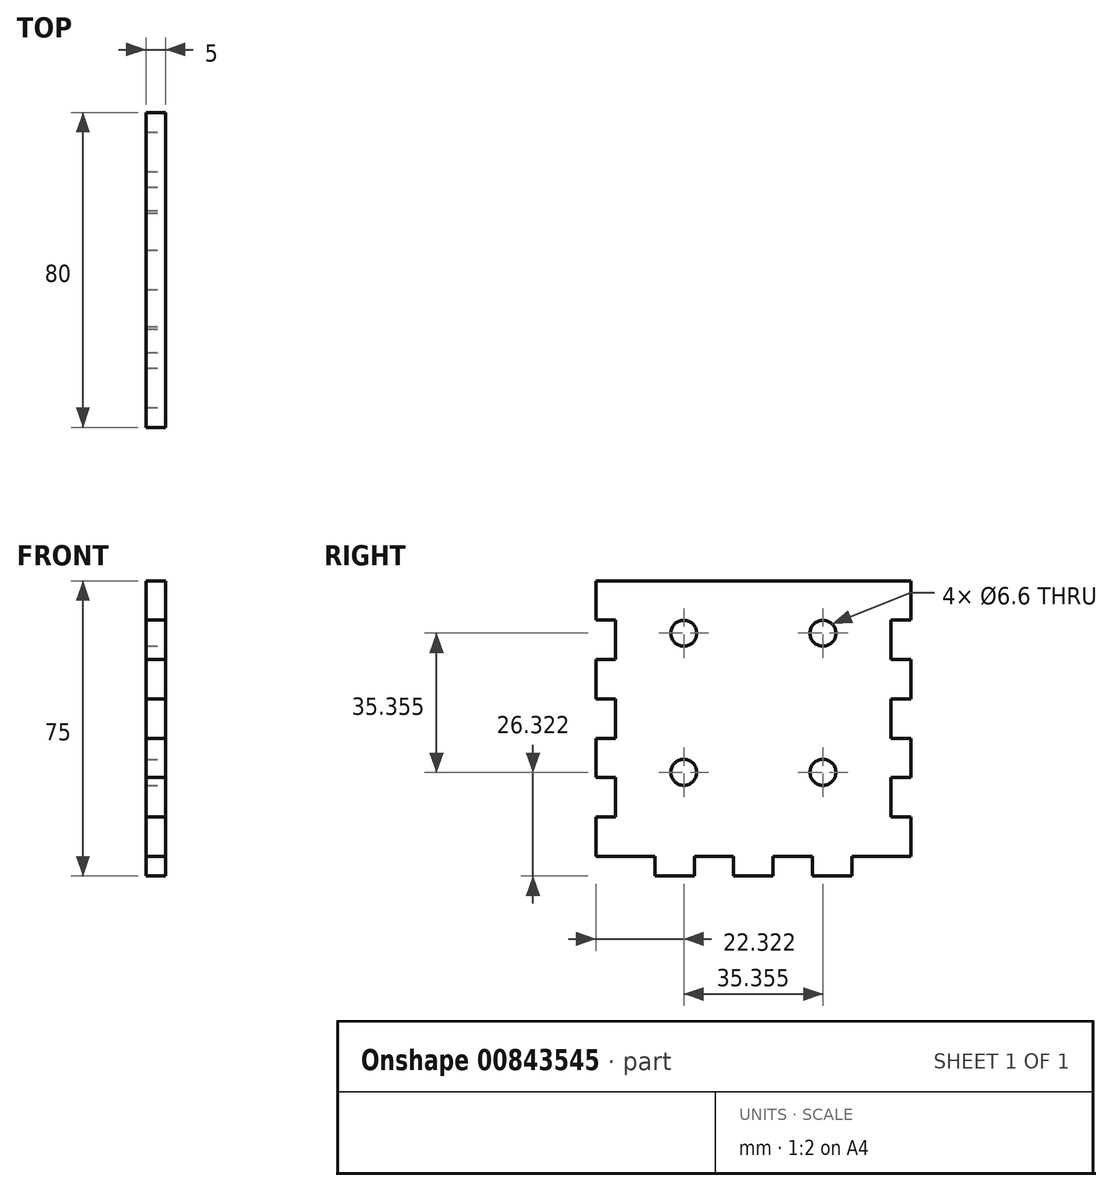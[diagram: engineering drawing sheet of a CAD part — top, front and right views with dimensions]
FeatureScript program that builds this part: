
annotation { "Feature Type Name" : "Feature", "Feature Type Description" : "" }
export const myFeature = defineFeature(function(context is Context, id is Id, definition is map)
    precondition{}
    {
        {
            var Q0;
            Q0=qCreatedBy(makeId("Right.planeOp"),FACE);
            var sketch = newSketch(context, id + "F0", { "sketchPlane" : qUnion([Q0])});
            skLineSegment(sketch, "E0.bottom", {"start": v(35, 35) * mm, "end": v(-35, 35) * mm});
            skLineSegment(sketch, "E0.top", {"start": v(35, -35) * mm, "end": v(-35, -35) * mm});
            skLineSegment(sketch, "E0.left", {"start": v(35, 35) * mm, "end": v(35, -35) * mm});
            skLineSegment(sketch, "E0.right", {"start": v(-35, 35) * mm, "end": v(-35, -35) * mm});
            skPoint(sketch, "E0.middle", {"position": v(0, 0) * mm});
            skSolve(sketch);
        }
        {
            var Q0;
            Q0 = qSketchRegion(id + "F0", true);
            extrude(context, id + "F1", {"entities" : qUnion([Q0]), "endBound" : BoundingType.SYMMETRIC, "depth" : 5 * mm, "offsetDistance" : 25 * mm});
        }
        {
            var Q0;
            Q0=makeQuery(id+"F1.opExtrude","CAP_FACE",FACE,{"disambiguationData":[OSD([sQuery(id+"F0.wireOp",EDGE,"E0.bottom"),sQuery(id+"F0.wireOp",EDGE,"E0.top"),sQuery(id+"F0.wireOp",EDGE,"E0.left"),sQuery(id+"F0.wireOp",EDGE,"E0.right")])],"isStart":false});
            var sketch = newSketch(context, id + "F2", { "sketchPlane" : qUnion([Q0])});
            skLineSegment(sketch, "E1.bottom", {"start": v(-25, -35) * mm, "end": v(-15, -35) * mm});
            skLineSegment(sketch, "E1.top", {"start": v(-25, -40) * mm, "end": v(-15, -40) * mm});
            skLineSegment(sketch, "E1.left", {"start": v(-25, -35) * mm, "end": v(-25, -40) * mm});
            skLineSegment(sketch, "E1.right", {"start": v(-15, -35) * mm, "end": v(-15, -40) * mm});
            skLineSegment(sketch, "E2.1.0.0", {"start": v(5, -35) * mm, "end": v(5, -40) * mm});
            skLineSegment(sketch, "E2.1.0.1", {"start": v(-5, -35) * mm, "end": v(-5, -40) * mm});
            skLineSegment(sketch, "E2.1.0.2", {"start": v(-5, -40) * mm, "end": v(5, -40) * mm});
            skLineSegment(sketch, "E2.1.0.3", {"start": v(-5, -35) * mm, "end": v(5, -35) * mm});
            skLineSegment(sketch, "E2.2.0.0", {"start": v(25, -35) * mm, "end": v(25, -40) * mm});
            skLineSegment(sketch, "E2.2.0.1", {"start": v(15, -35) * mm, "end": v(15, -40) * mm});
            skLineSegment(sketch, "E2.2.0.2", {"start": v(15, -40) * mm, "end": v(25, -40) * mm});
            skLineSegment(sketch, "E2.2.0.3", {"start": v(15, -35) * mm, "end": v(25, -35) * mm});
            skLineSegment(sketch, "E2.direction1", {"start": v(-25, -40) * mm, "end": v(-5, -40) * mm, "construction": true});
            skSolve(sketch);
        }
        {
            var Q0;
            Q0 = qSketchRegion(id + "F2", true);
            extrude(context, id + "F3", {"entities" : qUnion([Q0]), "operationType" : NewBodyOperationType.ADD, "oppositeDirection" : true, "depth" : 5 * mm, "offsetDistance" : 25 * mm});
        }
        {
            var Q0;
            {var subQ1=sQuery(id+"F2.wireOp",EDGE,"E1.bottom");Q0=makeQuery(id+"F2.imprint","IMPRINT",FACE,{"disambiguationData":[TD([[makeQuery(id+"F2.imprint","IMPRINT",EDGE,{"derivedFrom":subQ1}),-1.0]])]});}
            var sketch = newSketch(context, id + "F4", { "sketchPlane" : qUnion([Q0])});
            skLineSegment(sketch, "E3.bottom", {"start": v(-35, -35) * mm, "end": v(-40, -35) * mm});
            skLineSegment(sketch, "E3.top", {"start": v(-35, -25) * mm, "end": v(-40, -25) * mm});
            skLineSegment(sketch, "E3.left", {"start": v(-35, -35) * mm, "end": v(-35, -25) * mm});
            skLineSegment(sketch, "E3.right", {"start": v(-40, -35) * mm, "end": v(-40, -25) * mm});
            skLineSegment(sketch, "E4.0.1.0", {"start": v(-35, -15) * mm, "end": v(-35, -5) * mm});
            skLineSegment(sketch, "E4.0.1.1", {"start": v(-40, -15) * mm, "end": v(-40, -5) * mm});
            skLineSegment(sketch, "E4.0.1.2", {"start": v(-35, -15) * mm, "end": v(-40, -15) * mm});
            skLineSegment(sketch, "E4.0.1.3", {"start": v(-35, -5) * mm, "end": v(-40, -5) * mm});
            skLineSegment(sketch, "E4.0.2.0", {"start": v(-35, 5) * mm, "end": v(-35, 15) * mm});
            skLineSegment(sketch, "E4.0.2.1", {"start": v(-40, 5) * mm, "end": v(-40, 15) * mm});
            skLineSegment(sketch, "E4.0.2.2", {"start": v(-35, 5) * mm, "end": v(-40, 5) * mm});
            skLineSegment(sketch, "E4.0.2.3", {"start": v(-35, 15) * mm, "end": v(-40, 15) * mm});
            skLineSegment(sketch, "E4.0.3.0", {"start": v(-35, 25) * mm, "end": v(-35, 35) * mm});
            skLineSegment(sketch, "E4.0.3.1", {"start": v(-40, 25) * mm, "end": v(-40, 35) * mm});
            skLineSegment(sketch, "E4.0.3.2", {"start": v(-35, 25) * mm, "end": v(-40, 25) * mm});
            skLineSegment(sketch, "E4.0.3.3", {"start": v(-35, 35) * mm, "end": v(-40, 35) * mm});
            skLineSegment(sketch, "E4.direction1", {"start": v(-40, -35) * mm, "end": v(-15, -35) * mm, "construction": true});
            skLineSegment(sketch, "E4.direction2", {"start": v(-40, -35) * mm, "end": v(-40, -15) * mm, "construction": true});
            skLineSegment(sketch, "E5.1.0.0", {"start": v(40, 25) * mm, "end": v(40, 35) * mm});
            skLineSegment(sketch, "E5.1.0.1", {"start": v(40, 25) * mm, "end": v(35, 25) * mm});
            skLineSegment(sketch, "E5.1.0.2", {"start": v(40, -35) * mm, "end": v(35, -35) * mm});
            skLineSegment(sketch, "E5.1.0.3", {"start": v(40, 15) * mm, "end": v(35, 15) * mm});
            skLineSegment(sketch, "E5.1.0.4", {"start": v(40, -35) * mm, "end": v(40, -25) * mm});
            skLineSegment(sketch, "E5.1.0.5", {"start": v(35, -35) * mm, "end": v(35, -15) * mm, "construction": true});
            skLineSegment(sketch, "E5.1.0.6", {"start": v(40, 5) * mm, "end": v(40, 15) * mm});
            skLineSegment(sketch, "E5.1.0.7", {"start": v(40, -15) * mm, "end": v(40, -5) * mm});
            skLineSegment(sketch, "E5.1.0.8", {"start": v(40, -15) * mm, "end": v(35, -15) * mm});
            skLineSegment(sketch, "E5.1.0.9", {"start": v(35, 5) * mm, "end": v(35, 15) * mm});
            skLineSegment(sketch, "E5.1.0.10", {"start": v(40, 35) * mm, "end": v(35, 35) * mm});
            skLineSegment(sketch, "E5.1.0.11", {"start": v(40, -25) * mm, "end": v(35, -25) * mm});
            skLineSegment(sketch, "E5.1.0.12", {"start": v(35, -15) * mm, "end": v(35, -5) * mm});
            skLineSegment(sketch, "E5.1.0.13", {"start": v(40, 5) * mm, "end": v(35, 5) * mm});
            skLineSegment(sketch, "E5.1.0.14", {"start": v(40, -5) * mm, "end": v(35, -5) * mm});
            skLineSegment(sketch, "E5.1.0.15", {"start": v(35, 25) * mm, "end": v(35, 35) * mm});
            skLineSegment(sketch, "E5.1.0.16", {"start": v(35, -35) * mm, "end": v(35, -25) * mm});
            skLineSegment(sketch, "E5.direction1", {"start": v(-40, -35) * mm, "end": v(35, -35) * mm, "construction": true});
            skSolve(sketch);
        }
        {
            var Q0;
            Q0 = qSketchRegion(id + "F4", true);
            var Q1;
            Q1=makeQuery(id+"F3.boolean.opBoolean","MERGE",FACE,{"derivedFrom":[makeQuery(id+"F1.opExtrude","CAP_FACE",FACE,{"disambiguationData":[OSD([sQuery(id+"F0.wireOp",EDGE,"E0.bottom"),sQuery(id+"F0.wireOp",EDGE,"E0.top"),sQuery(id+"F0.wireOp",EDGE,"E0.left"),sQuery(id+"F0.wireOp",EDGE,"E0.right")])],"isStart":true}),makeQuery(id+"F3.opExtrude","CAP_FACE",FACE,{"disambiguationData":[OSD([sQuery(id+"F2.wireOp",EDGE,"E1.bottom"),sQuery(id+"F2.wireOp",EDGE,"E1.top"),sQuery(id+"F2.wireOp",EDGE,"E1.left"),sQuery(id+"F2.wireOp",EDGE,"E1.right")])],"isStart":false}),makeQuery(id+"F3.opExtrude","CAP_FACE",FACE,{"disambiguationData":[OSD([sQuery(id+"F2.wireOp",EDGE,"E2.1.0.0"),sQuery(id+"F2.wireOp",EDGE,"E2.1.0.1"),sQuery(id+"F2.wireOp",EDGE,"E2.1.0.2"),sQuery(id+"F2.wireOp",EDGE,"E2.1.0.3")])],"isStart":false}),makeQuery(id+"F3.opExtrude","CAP_FACE",FACE,{"disambiguationData":[OSD([sQuery(id+"F2.wireOp",EDGE,"E2.2.0.0"),sQuery(id+"F2.wireOp",EDGE,"E2.2.0.1"),sQuery(id+"F2.wireOp",EDGE,"E2.2.0.2"),sQuery(id+"F2.wireOp",EDGE,"E2.2.0.3")])],"isStart":false})]});
            extrude(context, id + "F5", {"entities" : qUnion([Q0]), "operationType" : NewBodyOperationType.ADD, "endBound" : BoundingType.UP_TO_SURFACE, "oppositeDirection" : true, "depth" : 25 * mm, "endBoundEntityFace" : qUnion([Q1]), "offsetDistance" : 25 * mm});
        }
        {
            var Q0;
            {var subQ1=sQuery(id+"F2.wireOp",EDGE,"E1.bottom");Q0=makeQuery(id+"F2.imprint","IMPRINT",FACE,{"disambiguationData":[TD([[makeQuery(id+"F2.imprint","IMPRINT",EDGE,{"derivedFrom":subQ1}),-1.0]])]});}
            var sketch = newSketch(context, id + "F6", { "sketchPlane" : qUnion([Q0])});
            skCircle(sketch, "E6", {"center": v(0, 4) * mm, "radius": 25 * mm, "construction": true});
            skLineSegment(sketch, "E7.bottom", {"start": v(17.68, 21.68) * mm, "end": v(-17.68, 21.68) * mm, "construction": true});
            skLineSegment(sketch, "E7.top", {"start": v(17.68, -13.68) * mm, "end": v(-17.68, -13.68) * mm, "construction": true});
            skLineSegment(sketch, "E7.left", {"start": v(17.68, 21.68) * mm, "end": v(17.68, -13.68) * mm, "construction": true});
            skLineSegment(sketch, "E7.right", {"start": v(-17.68, 21.68) * mm, "end": v(-17.68, -13.68) * mm, "construction": true});
            skSolve(sketch);
        }
        {
            var Q0;
            Q0=sQuery(id+"F6.wireOp",VERTEX,"E7.bottom.end");
            var Q1;
            Q1=sQuery(id+"F6.wireOp",VERTEX,"E7.bottom.start");
            var Q2;
            Q2=sQuery(id+"F6.wireOp",VERTEX,"E7.top.start");
            var Q3;
            Q3=sQuery(id+"F6.wireOp",VERTEX,"E7.top.end");
            var Q4;
            Q4=makeQuery(id+"F1.opExtrude","SWEPT_BODY",BODY,{"disambiguationData":[OSD([sQuery(id+"F0.wireOp",EDGE,"E0.bottom"),sQuery(id+"F0.wireOp",EDGE,"E0.top"),sQuery(id+"F0.wireOp",EDGE,"E0.left"),sQuery(id+"F0.wireOp",EDGE,"E0.right")])]});
            hole(context, id + "F7", {"style" : HoleStyle.SIMPLE, "endStyle" : HoleEndStyle.THROUGH, "standardTappedOrClearance" : lookupTablePath({ "fit" : "Normal", "standard" : "ISO", "size" : "M6", "type" : "Clearance" }), "standardBlindInLast" : lookupTablePath({ "fit" : "Standard", "standard" : "ISO", "size" : "M6", "type" : "Clearance" }), "holeDiameter" : 6.6 * mm, "majorDiameter" : 5 * mm, "isTappedThrough" : true, "tappedDepth" : 12 * mm, "tapClearance" : 3, "locations" : qUnion([Q0, Q1, Q2, Q3]), "scope" : qUnion([Q4])});
        }
    });
